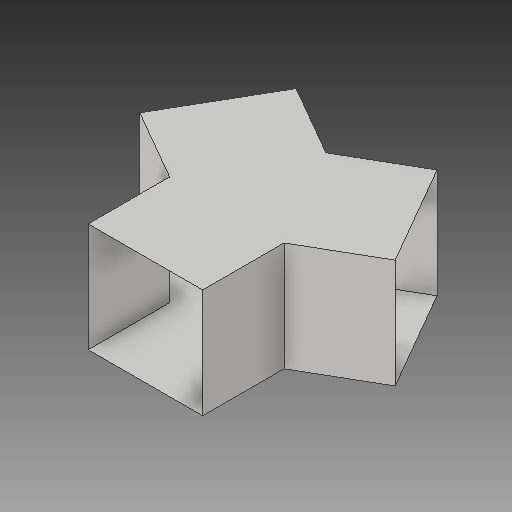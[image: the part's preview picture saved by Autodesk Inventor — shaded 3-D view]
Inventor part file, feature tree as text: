
AUTODESK INVENTOR PART (.ipt)
format: ipt  version: 2017 (Build 210142000, 142)  size: 103,936 bytes
history: native  units: in
note: dims shown in document units (in); Inventor stores cm internally (conversion verified against a paired STEP export)
features: extrude x1, pattern_circular x1, other x1, sketch x1
ambient origin geometry x8: Origin, YZ Plane, XZ Plane, XY Plane, X Axis, Y Axis, Z Axis, Center Point
bodies: Solid1 (feature_tree)
feature tree (4):
  extrude  "corridor"  Depth=6.6667in
  pattern_circular  "made the Y"  [2 undecoded]
  other  "removed ends"
  sketch  "Sketch1"  dims[d0=7.0in d1=6.6667in d2=7.0in d3=0.0in d4=1.1811in d5=360.0deg]
note: 2 required parameter values undecoded (feature->parameter linkage not recoverable at this tier; creation-order binding heuristic only, values carry confidence <= 0.55)
